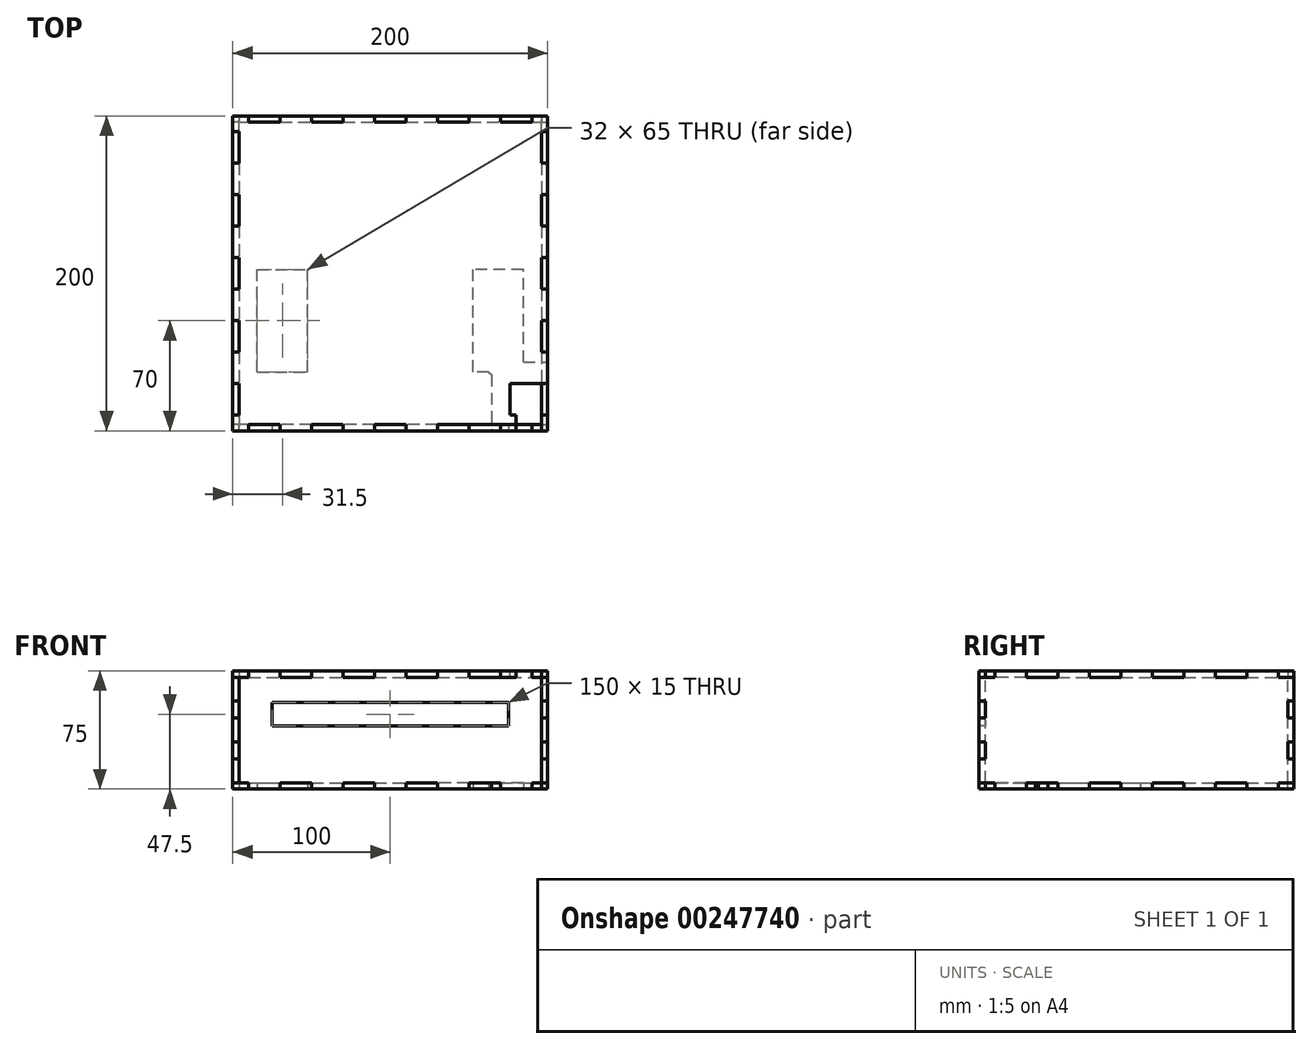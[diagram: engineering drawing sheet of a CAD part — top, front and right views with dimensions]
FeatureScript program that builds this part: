
annotation { "Feature Type Name" : "Feature", "Feature Type Description" : "" }
export const myFeature = defineFeature(function(context is Context, id is Id, definition is map)
    precondition{}
    {
        {
            var Q0;
            Q0=qCreatedBy(makeId("Top.planeOp"),FACE);
            var sketch = newSketch(context, id + "F0", { "sketchPlane" : qUnion([Q0])});
            skLineSegment(sketch, "E0.bottom", {"start": v(100, -100) * mm, "end": v(-100, -100) * mm});
            skLineSegment(sketch, "E0.top", {"start": v(100, 100) * mm, "end": v(-100, 100) * mm});
            skLineSegment(sketch, "E0.left", {"start": v(100, -100) * mm, "end": v(100, 100) * mm});
            skLineSegment(sketch, "E0.right", {"start": v(-100, -100) * mm, "end": v(-100, 100) * mm});
            skPoint(sketch, "E0.middle", {"position": v(0, 0) * mm});
            skLineSegment(sketch, "E1", {"start": v(0, 100) * mm, "end": v(0, 96) * mm});
            skLineSegment(sketch, "E2", {"start": v(0, 96) * mm, "end": v(10, 96) * mm});
            skLineSegment(sketch, "E3", {"start": v(10, 96) * mm, "end": v(10, 100) * mm});
            skLineSegment(sketch, "E4.MirrorCS", {"start": v(0, 96) * mm, "end": v(-10, 96) * mm});
            skLineSegment(sketch, "E5.MirrorCS", {"start": v(-10, 96) * mm, "end": v(-10, 100) * mm});
            skLineSegment(sketch, "E6.1.0.0", {"start": v(30, 96) * mm, "end": v(30, 100) * mm});
            skLineSegment(sketch, "E6.1.0.1", {"start": v(40, 96) * mm, "end": v(30, 96) * mm});
            skLineSegment(sketch, "E6.1.0.2", {"start": v(40, 96) * mm, "end": v(50, 96) * mm});
            skLineSegment(sketch, "E6.1.0.3", {"start": v(50, 96) * mm, "end": v(50, 100) * mm});
            skLineSegment(sketch, "E6.2.0.0", {"start": v(70, 96) * mm, "end": v(70, 100) * mm});
            skLineSegment(sketch, "E6.2.0.1", {"start": v(80, 96) * mm, "end": v(70, 96) * mm});
            skLineSegment(sketch, "E6.2.0.2", {"start": v(80, 96) * mm, "end": v(90, 96) * mm});
            skLineSegment(sketch, "E6.2.0.3", {"start": v(90, 96) * mm, "end": v(90, 100) * mm});
            skLineSegment(sketch, "E6.direction1", {"start": v(-10, 96) * mm, "end": v(30, 96) * mm, "construction": true});
            skLineSegment(sketch, "E7.MirrorCS", {"start": v(-50, 96) * mm, "end": v(-50, 100) * mm});
            skLineSegment(sketch, "E8.MirrorCS", {"start": v(-30, 96) * mm, "end": v(-30, 100) * mm});
            skLineSegment(sketch, "E9.MirrorCS", {"start": v(-70, 96) * mm, "end": v(-70, 100) * mm});
            skLineSegment(sketch, "E10.MirrorCS", {"start": v(-90, 96) * mm, "end": v(-90, 100) * mm});
            skLineSegment(sketch, "E11.MirrorCS", {"start": v(-40, 96) * mm, "end": v(-30, 96) * mm});
            skLineSegment(sketch, "E12.MirrorCS", {"start": v(-40, 96) * mm, "end": v(-50, 96) * mm});
            skLineSegment(sketch, "E13.MirrorCS", {"start": v(-80, 96) * mm, "end": v(-70, 96) * mm});
            skLineSegment(sketch, "E14.MirrorCS", {"start": v(-80, 96) * mm, "end": v(-90, 96) * mm});
            skLineSegment(sketch, "E15", {"start": v(-100, 100) * mm, "end": v(100, -100) * mm});
            skLineSegment(sketch, "E16.MirrorCS", {"start": v(-96, 10) * mm, "end": v(-100, 10) * mm});
            skLineSegment(sketch, "E17.MirrorCS", {"start": v(-100, 0) * mm, "end": v(-96, 0) * mm});
            skLineSegment(sketch, "E18.MirrorCS", {"start": v(-96, -30) * mm, "end": v(-100, -30) * mm});
            skLineSegment(sketch, "E19.MirrorCS", {"start": v(-96, -10) * mm, "end": v(-100, -10) * mm});
            skLineSegment(sketch, "E20.MirrorCS", {"start": v(-96, 0) * mm, "end": v(-96, 10) * mm});
            skLineSegment(sketch, "E21.MirrorCS", {"start": v(-96, 50) * mm, "end": v(-100, 50) * mm});
            skLineSegment(sketch, "E22.MirrorCS", {"start": v(-96, 90) * mm, "end": v(-100, 90) * mm});
            skLineSegment(sketch, "E23.MirrorCS", {"start": v(-96, -90) * mm, "end": v(-100, -90) * mm});
            skLineSegment(sketch, "E24.MirrorCS", {"start": v(-96, -50) * mm, "end": v(-100, -50) * mm});
            skLineSegment(sketch, "E25.MirrorCS", {"start": v(-96, 30) * mm, "end": v(-100, 30) * mm});
            skLineSegment(sketch, "E26.MirrorCS", {"start": v(-96, 70) * mm, "end": v(-100, 70) * mm});
            skLineSegment(sketch, "E27.MirrorCS", {"start": v(-96, -70) * mm, "end": v(-100, -70) * mm});
            skLineSegment(sketch, "E28.MirrorCS", {"start": v(-96, -40) * mm, "end": v(-96, -30) * mm});
            skLineSegment(sketch, "E29.MirrorCS", {"start": v(-96, 0) * mm, "end": v(-96, -10) * mm});
            skLineSegment(sketch, "E30.MirrorCS", {"start": v(-96, 10) * mm, "end": v(-96, -30) * mm, "construction": true});
            skLineSegment(sketch, "E31.MirrorCS", {"start": v(-96, -80) * mm, "end": v(-96, -90) * mm});
            skLineSegment(sketch, "E32.MirrorCS", {"start": v(-96, 40) * mm, "end": v(-96, 50) * mm});
            skLineSegment(sketch, "E33.MirrorCS", {"start": v(-96, 80) * mm, "end": v(-96, 70) * mm});
            skLineSegment(sketch, "E34.MirrorCS", {"start": v(-96, -40) * mm, "end": v(-96, -50) * mm});
            skLineSegment(sketch, "E35.MirrorCS", {"start": v(-96, 80) * mm, "end": v(-96, 90) * mm});
            skLineSegment(sketch, "E36.MirrorCS", {"start": v(-96, 40) * mm, "end": v(-96, 30) * mm});
            skLineSegment(sketch, "E37.MirrorCS", {"start": v(-96, -80) * mm, "end": v(-96, -70) * mm});
            skLineSegment(sketch, "E38.MirrorCS", {"start": v(96, 10) * mm, "end": v(100, 10) * mm});
            skLineSegment(sketch, "E39.MirrorCS", {"start": v(96, 0) * mm, "end": v(96, 10) * mm});
            skLineSegment(sketch, "E40.MirrorCS", {"start": v(100, 0) * mm, "end": v(96, 0) * mm});
            skLineSegment(sketch, "E41.MirrorCS", {"start": v(96, -30) * mm, "end": v(100, -30) * mm});
            skLineSegment(sketch, "E42.MirrorCS", {"start": v(96, -40) * mm, "end": v(96, -30) * mm});
            skLineSegment(sketch, "E43.MirrorCS", {"start": v(96, 50) * mm, "end": v(100, 50) * mm});
            skLineSegment(sketch, "E44.MirrorCS", {"start": v(96, 30) * mm, "end": v(100, 30) * mm});
            skLineSegment(sketch, "E45.MirrorCS", {"start": v(96, 80) * mm, "end": v(96, 90) * mm});
            skLineSegment(sketch, "E46.MirrorCS", {"start": v(96, -50) * mm, "end": v(100, -50) * mm});
            skLineSegment(sketch, "E47.MirrorCS", {"start": v(96, 40) * mm, "end": v(96, 50) * mm});
            skLineSegment(sketch, "E48.MirrorCS", {"start": v(96, -70) * mm, "end": v(100, -70) * mm});
            skLineSegment(sketch, "E49.MirrorCS", {"start": v(96, -10) * mm, "end": v(100, -10) * mm});
            skLineSegment(sketch, "E50.MirrorCS", {"start": v(96, -90) * mm, "end": v(100, -90) * mm});
            skLineSegment(sketch, "E51.MirrorCS", {"start": v(96, -80) * mm, "end": v(96, -90) * mm});
            skLineSegment(sketch, "E52.MirrorCS", {"start": v(96, 70) * mm, "end": v(100, 70) * mm});
            skLineSegment(sketch, "E53.MirrorCS", {"start": v(96, 80) * mm, "end": v(96, 70) * mm});
            skLineSegment(sketch, "E54.MirrorCS", {"start": v(96, 90) * mm, "end": v(100, 90) * mm});
            skLineSegment(sketch, "E55.MirrorCS", {"start": v(96, -40) * mm, "end": v(96, -50) * mm});
            skLineSegment(sketch, "E56.MirrorCS", {"start": v(96, 0) * mm, "end": v(96, -10) * mm});
            skLineSegment(sketch, "E57.MirrorCS", {"start": v(96, -80) * mm, "end": v(96, -70) * mm});
            skLineSegment(sketch, "E58.MirrorCS", {"start": v(96, 40) * mm, "end": v(96, 30) * mm});
            skLineSegment(sketch, "E59.MirrorCS", {"start": v(96, 10) * mm, "end": v(96, -30) * mm, "construction": true});
            skLineSegment(sketch, "E60", {"start": v(0, -100) * mm, "end": v(0, -96) * mm});
            skLineSegment(sketch, "E61", {"start": v(0, -96) * mm, "end": v(10, -96) * mm});
            skLineSegment(sketch, "E62", {"start": v(10, -96) * mm, "end": v(10, -100) * mm});
            skLineSegment(sketch, "E63.MirrorCS", {"start": v(0, -96) * mm, "end": v(-10, -96) * mm});
            skLineSegment(sketch, "E64.MirrorCS", {"start": v(-10, -96) * mm, "end": v(-10, -100) * mm});
            skLineSegment(sketch, "E65.1.0.0", {"start": v(30, -96) * mm, "end": v(30, -100) * mm});
            skLineSegment(sketch, "E65.1.0.1", {"start": v(40, -96) * mm, "end": v(30, -96) * mm});
            skLineSegment(sketch, "E65.1.0.2", {"start": v(40, -96) * mm, "end": v(50, -96) * mm});
            skLineSegment(sketch, "E65.1.0.3", {"start": v(50, -96) * mm, "end": v(50, -100) * mm});
            skLineSegment(sketch, "E65.2.0.0", {"start": v(70, -96) * mm, "end": v(70, -100) * mm});
            skLineSegment(sketch, "E65.2.0.1", {"start": v(80, -96) * mm, "end": v(70, -96) * mm});
            skLineSegment(sketch, "E65.2.0.2", {"start": v(80, -96) * mm, "end": v(90, -96) * mm});
            skLineSegment(sketch, "E65.2.0.3", {"start": v(90, -96) * mm, "end": v(90, -100) * mm});
            skLineSegment(sketch, "E65.direction1", {"start": v(-10, -100) * mm, "end": v(30, -100) * mm, "construction": true});
            skLineSegment(sketch, "E66.MirrorCS", {"start": v(-40, -96) * mm, "end": v(-50, -96) * mm});
            skLineSegment(sketch, "E67.MirrorCS", {"start": v(-40, -96) * mm, "end": v(-30, -96) * mm});
            skLineSegment(sketch, "E68.MirrorCS", {"start": v(-80, -96) * mm, "end": v(-70, -96) * mm});
            skLineSegment(sketch, "E69.MirrorCS", {"start": v(-80, -96) * mm, "end": v(-90, -96) * mm});
            skLineSegment(sketch, "E70.MirrorCS", {"start": v(-70, -96) * mm, "end": v(-70, -100) * mm});
            skLineSegment(sketch, "E71.MirrorCS", {"start": v(-90, -96) * mm, "end": v(-90, -100) * mm});
            skLineSegment(sketch, "E72.MirrorCS", {"start": v(-30, -96) * mm, "end": v(-30, -100) * mm});
            skLineSegment(sketch, "E73.MirrorCS", {"start": v(-50, -96) * mm, "end": v(-50, -100) * mm});
            skLineSegment(sketch, "E74.bottom", {"start": v(84.5, -62.5) * mm, "end": v(52.5, -62.5) * mm});
            skLineSegment(sketch, "E74.top", {"start": v(84.5, 2.5) * mm, "end": v(52.5, 2.5) * mm});
            skLineSegment(sketch, "E74.left", {"start": v(84.5, -62.5) * mm, "end": v(84.5, 2.5) * mm});
            skLineSegment(sketch, "E74.right", {"start": v(52.5, -62.5) * mm, "end": v(52.5, 2.5) * mm});
            skPoint(sketch, "E74.middle", {"position": v(68.5, -30) * mm});
            skLineSegment(sketch, "E75", {"start": v(0, 96) * mm, "end": v(0, -96) * mm});
            skLineSegment(sketch, "E76.MirrorCS", {"start": v(-52.5, -62.5) * mm, "end": v(-52.5, 2.5) * mm});
            skLineSegment(sketch, "E77.MirrorCS", {"start": v(-84.5, 2.5) * mm, "end": v(-52.5, 2.5) * mm});
            skLineSegment(sketch, "E78.MirrorCS", {"start": v(-84.5, -62.5) * mm, "end": v(-84.5, 2.5) * mm});
            skLineSegment(sketch, "E79.MirrorCS", {"start": v(-84.5, -62.5) * mm, "end": v(-52.5, -62.5) * mm});
            skLineSegment(sketch, "E80", {"start": v(64.36, -62.5) * mm, "end": v(64.36, -100) * mm});
            skLineSegment(sketch, "E81", {"start": v(84.5, -56.4) * mm, "end": v(100, -56.4) * mm});
            skSolve(sketch);
        }
        {
            var Q0;
            Q0=makeQuery(id+"F0.imprint","IMPRINT",FACE,{"disambiguationData":[TD([[makeQuery(id+"F0.imprint","IMPRINT",EDGE,{"derivedFrom":sQuery(id+"F0.wireOp",EDGE,"E2")}),-1.0]])]});
            var Q1;
            {var subQ15=sQuery(id+"F0.wireOp",EDGE,"E15");Q1=makeQuery(id+"F0.imprint","IMPRINT",FACE,{"disambiguationData":[TD([[makeQuery(id+"F0.imprint","IMPRINT",EDGE,{"derivedFrom":subQ15}),-1.0]])]});}
            var Q2;
            {var subQ5=sQuery(id+"F0.wireOp",EDGE,"E16.MirrorCS");Q2=makeQuery(id+"F0.imprint","IMPRINT",FACE,{"disambiguationData":[TD([[makeQuery(id+"F0.imprint","IMPRINT",EDGE,{"derivedFrom":subQ5}),-1.0]])]});}
            var Q3;
            {var subQ5=sQuery(id+"F0.wireOp",EDGE,"E5.MirrorCS");Q3=makeQuery(id+"F0.imprint","IMPRINT",FACE,{"disambiguationData":[TD([[makeQuery(id+"F0.imprint","IMPRINT",EDGE,{"derivedFrom":subQ5}),1.0]])]});}
            extrude(context, id + "F1", {"entities" : qUnion([Q0, Q1, Q2, Q3]), "depth" : 4 * mm});
        }
        {
            var Q0;
            Q0=makeQuery(id+"F1.opExtrude","SWEPT_FACE",FACE,{"disambiguationData":[OSD([sQuery(id+"F0.wireOp",EDGE,"E39.MirrorCS"),sQuery(id+"F0.wireOp",EDGE,"E56.MirrorCS")])]});
            var sketch = newSketch(context, id + "F2", { "sketchPlane" : qUnion([Q0])});
            skLineSegment(sketch, "E82.0.0", {"start": v(-90, 0) * mm, "end": v(-70, 0) * mm});
            skLineSegment(sketch, "E82.0.1", {"start": v(-70, 0) * mm, "end": v(-70, 4) * mm});
            skLineSegment(sketch, "E82.0.2", {"start": v(-70, 4) * mm, "end": v(-90, 4) * mm});
            skLineSegment(sketch, "E82.0.3", {"start": v(-90, 4) * mm, "end": v(-90, 0) * mm});
            skLineSegment(sketch, "E83.0.0", {"start": v(-50, 0) * mm, "end": v(-30, 0) * mm});
            skLineSegment(sketch, "E83.0.1", {"start": v(-30, 0) * mm, "end": v(-30, 4) * mm});
            skLineSegment(sketch, "E83.0.2", {"start": v(-30, 4) * mm, "end": v(-50, 4) * mm});
            skLineSegment(sketch, "E83.0.3", {"start": v(-50, 4) * mm, "end": v(-50, 0) * mm});
            skLineSegment(sketch, "E84.0.0", {"start": v(-10, 0) * mm, "end": v(10, 0) * mm});
            skLineSegment(sketch, "E84.0.1", {"start": v(10, 0) * mm, "end": v(10, 4) * mm});
            skLineSegment(sketch, "E84.0.2", {"start": v(10, 4) * mm, "end": v(-10, 4) * mm});
            skLineSegment(sketch, "E84.0.3", {"start": v(-10, 4) * mm, "end": v(-10, 0) * mm});
            skLineSegment(sketch, "E85.0.0", {"start": v(30, 0) * mm, "end": v(50, 0) * mm});
            skLineSegment(sketch, "E85.0.1", {"start": v(50, 0) * mm, "end": v(50, 4) * mm});
            skLineSegment(sketch, "E85.0.2", {"start": v(50, 4) * mm, "end": v(30, 4) * mm});
            skLineSegment(sketch, "E85.0.3", {"start": v(30, 4) * mm, "end": v(30, 0) * mm});
            skLineSegment(sketch, "E86.0.0", {"start": v(70, 0) * mm, "end": v(90, 0) * mm});
            skLineSegment(sketch, "E86.0.1", {"start": v(90, 0) * mm, "end": v(90, 4) * mm});
            skLineSegment(sketch, "E86.0.2", {"start": v(90, 4) * mm, "end": v(70, 4) * mm});
            skLineSegment(sketch, "E86.0.3", {"start": v(70, 4) * mm, "end": v(70, 0) * mm});
            skLineSegment(sketch, "E87.0.1", {"start": v(96, 0) * mm, "end": v(96, 4) * mm});
            skLineSegment(sketch, "E87.0.3", {"start": v(96, 4) * mm, "end": v(96, 0) * mm});
            skLineSegment(sketch, "E88.0.1", {"start": v(-96, 0) * mm, "end": v(-96, 4) * mm});
            skLineSegment(sketch, "E88.0.3", {"start": v(-96, 4) * mm, "end": v(-96, 0) * mm});
            skLineSegment(sketch, "E89.0.1", {"start": v(70, 4) * mm, "end": v(90, 4) * mm});
            skLineSegment(sketch, "E89.0.3", {"start": v(90, 4) * mm, "end": v(100, 4) * mm});
            skLineSegment(sketch, "E89.0.5", {"start": v(100, 4) * mm, "end": v(96, 4) * mm});
            skLineSegment(sketch, "E89.0.7", {"start": v(96, 4) * mm, "end": v(100, 4) * mm});
            skLineSegment(sketch, "E89.0.9", {"start": v(100, 4) * mm, "end": v(96, 4) * mm});
            skLineSegment(sketch, "E89.0.11", {"start": v(96, 4) * mm, "end": v(100, 4) * mm});
            skLineSegment(sketch, "E89.0.13", {"start": v(100, 4) * mm, "end": v(96, 4) * mm});
            skLineSegment(sketch, "E89.0.15", {"start": v(96, 4) * mm, "end": v(100, 4) * mm});
            skLineSegment(sketch, "E89.0.17", {"start": v(100, 4) * mm, "end": v(96, 4) * mm});
            skLineSegment(sketch, "E89.0.19", {"start": v(96, 4) * mm, "end": v(100, 4) * mm});
            skLineSegment(sketch, "E89.0.21", {"start": v(100, 4) * mm, "end": v(96, 4) * mm});
            skLineSegment(sketch, "E89.0.23", {"start": v(96, 4) * mm, "end": v(100, 4) * mm});
            skLineSegment(sketch, "E89.0.25", {"start": v(100, 4) * mm, "end": v(90, 4) * mm});
            skLineSegment(sketch, "E89.0.29", {"start": v(70, 4) * mm, "end": v(50, 4) * mm});
            skLineSegment(sketch, "E89.0.33", {"start": v(30, 4) * mm, "end": v(10, 4) * mm});
            skLineSegment(sketch, "E89.0.37", {"start": v(-10, 4) * mm, "end": v(-30, 4) * mm});
            skLineSegment(sketch, "E89.0.41", {"start": v(-50, 4) * mm, "end": v(-70, 4) * mm});
            skLineSegment(sketch, "E89.0.45", {"start": v(-90, 4) * mm, "end": v(-100, 4) * mm});
            skLineSegment(sketch, "E89.0.47", {"start": v(-100, 4) * mm, "end": v(-96, 4) * mm});
            skLineSegment(sketch, "E89.0.49", {"start": v(-96, 4) * mm, "end": v(-100, 4) * mm});
            skLineSegment(sketch, "E89.0.51", {"start": v(-100, 4) * mm, "end": v(-96, 4) * mm});
            skLineSegment(sketch, "E89.0.53", {"start": v(-96, 4) * mm, "end": v(-100, 4) * mm});
            skLineSegment(sketch, "E89.0.55", {"start": v(-100, 4) * mm, "end": v(-96, 4) * mm});
            skLineSegment(sketch, "E89.0.57", {"start": v(-96, 4) * mm, "end": v(-100, 4) * mm});
            skLineSegment(sketch, "E89.0.59", {"start": v(-100, 4) * mm, "end": v(-96, 4) * mm});
            skLineSegment(sketch, "E89.0.61", {"start": v(-96, 4) * mm, "end": v(-100, 4) * mm});
            skLineSegment(sketch, "E89.0.63", {"start": v(-100, 4) * mm, "end": v(-96, 4) * mm});
            skLineSegment(sketch, "E89.0.65", {"start": v(-96, 4) * mm, "end": v(-100, 4) * mm});
            skLineSegment(sketch, "E89.0.67", {"start": v(-100, 4) * mm, "end": v(-90, 4) * mm});
            skLineSegment(sketch, "E89.0.69", {"start": v(-90, 4) * mm, "end": v(-70, 4) * mm});
            skLineSegment(sketch, "E89.0.71", {"start": v(-50, 4) * mm, "end": v(-50, 4) * mm});
            skLineSegment(sketch, "E89.0.73", {"start": v(-50, 4) * mm, "end": v(-30, 4) * mm});
            skLineSegment(sketch, "E89.0.75", {"start": v(-30, 4) * mm, "end": v(-10, 4) * mm});
            skLineSegment(sketch, "E89.0.77", {"start": v(-10, 4) * mm, "end": v(10, 4) * mm});
            skLineSegment(sketch, "E89.0.79", {"start": v(10, 4) * mm, "end": v(30, 4) * mm});
            skLineSegment(sketch, "E89.0.81", {"start": v(30, 4) * mm, "end": v(50, 4) * mm});
            skLineSegment(sketch, "E89.0.83", {"start": v(50, 4) * mm, "end": v(70, 4) * mm});
            skLineSegment(sketch, "E90.bottom", {"start": v(-96, 4) * mm, "end": v(96, 4) * mm});
            skLineSegment(sketch, "E90.top", {"start": v(-96, 75) * mm, "end": v(96, 75) * mm});
            skLineSegment(sketch, "E90.left", {"start": v(-96, 4) * mm, "end": v(-96, 75) * mm});
            skLineSegment(sketch, "E90.right", {"start": v(96, 4) * mm, "end": v(96, 75) * mm});
            skLineSegment(sketch, "E91", {"start": v(96, 37.5) * mm, "end": v(-96, 37.5) * mm});
            skLineSegment(sketch, "E92.MirrorCS", {"start": v(-90, 71) * mm, "end": v(-90, 75) * mm});
            skLineSegment(sketch, "E93.MirrorCS", {"start": v(-30, 75) * mm, "end": v(-30, 71) * mm});
            skLineSegment(sketch, "E94.MirrorCS", {"start": v(-10, 71) * mm, "end": v(-10, 75) * mm});
            skLineSegment(sketch, "E95.MirrorCS", {"start": v(10, 75) * mm, "end": v(10, 71) * mm});
            skLineSegment(sketch, "E96.MirrorCS", {"start": v(30, 71) * mm, "end": v(30, 75) * mm});
            skLineSegment(sketch, "E97.MirrorCS", {"start": v(50, 75) * mm, "end": v(50, 71) * mm});
            skLineSegment(sketch, "E98.MirrorCS", {"start": v(70, 71) * mm, "end": v(70, 75) * mm});
            skLineSegment(sketch, "E99.MirrorCS", {"start": v(90, 75) * mm, "end": v(90, 71) * mm});
            skLineSegment(sketch, "E100.MirrorCS", {"start": v(-70, 75) * mm, "end": v(-70, 71) * mm});
            skLineSegment(sketch, "E101.MirrorCS", {"start": v(-50, 71) * mm, "end": v(-50, 75) * mm});
            skLineSegment(sketch, "E102", {"start": v(-90, 71) * mm, "end": v(-70, 71) * mm});
            skLineSegment(sketch, "E103", {"start": v(-50, 71) * mm, "end": v(-30, 71) * mm});
            skLineSegment(sketch, "E104", {"start": v(-10, 71) * mm, "end": v(10, 71) * mm});
            skLineSegment(sketch, "E105", {"start": v(30, 71) * mm, "end": v(50, 71) * mm});
            skLineSegment(sketch, "E106", {"start": v(70, 71) * mm, "end": v(90, 71) * mm});
            skLineSegment(sketch, "E107", {"start": v(-70, 71) * mm, "end": v(-50, 71) * mm});
            skLineSegment(sketch, "E108", {"start": v(-30, 71) * mm, "end": v(-10, 71) * mm});
            skLineSegment(sketch, "E109", {"start": v(10, 71) * mm, "end": v(30, 71) * mm});
            skLineSegment(sketch, "E110", {"start": v(50, 71) * mm, "end": v(70, 71) * mm});
            skLineSegment(sketch, "E111", {"start": v(-90, 71) * mm, "end": v(-96, 71) * mm});
            skLineSegment(sketch, "E112", {"start": v(90, 71) * mm, "end": v(96, 71) * mm});
            skSolve(sketch);
        }
        {
            var Q0;
            {var subQ7=sQuery(id+"F2.wireOp",EDGE,"E91");Q0=makeQuery(id+"F2.imprint","IMPRINT",FACE,{"disambiguationData":[TD([[makeQuery(id+"F2.imprint","IMPRINT",EDGE,{"derivedFrom":subQ7}),1.0]])]});}
            var Q1;
            {var subQ0=sQuery(id+"F2.wireOp",EDGE,"E91");Q1=makeQuery(id+"F2.imprint","IMPRINT",FACE,{"disambiguationData":[TD([[makeQuery(id+"F2.imprint","IMPRINT",EDGE,{"derivedFrom":subQ0}),-1.0]])]});}
            var Q2;
            {var subQ0=sQuery(id+"F2.wireOp",EDGE,"E92.MirrorCS");Q2=makeQuery(id+"F2.imprint","IMPRINT",FACE,{"disambiguationData":[TD([[makeQuery(id+"F2.imprint","IMPRINT",EDGE,{"derivedFrom":subQ0}),-1.0]])]});}
            var Q3;
            {var subQ0=sQuery(id+"F2.wireOp",EDGE,"E93.MirrorCS");Q3=makeQuery(id+"F2.imprint","IMPRINT",FACE,{"disambiguationData":[TD([[makeQuery(id+"F2.imprint","IMPRINT",EDGE,{"derivedFrom":subQ0}),-1.0]])]});}
            var Q4;
            {var subQ0=sQuery(id+"F2.wireOp",EDGE,"E94.MirrorCS");Q4=makeQuery(id+"F2.imprint","IMPRINT",FACE,{"disambiguationData":[TD([[makeQuery(id+"F2.imprint","IMPRINT",EDGE,{"derivedFrom":subQ0}),-1.0]])]});}
            var Q5;
            {var subQ0=sQuery(id+"F2.wireOp",EDGE,"E96.MirrorCS");Q5=makeQuery(id+"F2.imprint","IMPRINT",FACE,{"disambiguationData":[TD([[makeQuery(id+"F2.imprint","IMPRINT",EDGE,{"derivedFrom":subQ0}),-1.0]])]});}
            var Q6;
            {var subQ0=sQuery(id+"F2.wireOp",EDGE,"E98.MirrorCS");Q6=makeQuery(id+"F2.imprint","IMPRINT",FACE,{"disambiguationData":[TD([[makeQuery(id+"F2.imprint","IMPRINT",EDGE,{"derivedFrom":subQ0}),-1.0]])]});}
            var Q7;
            Q7=makeQuery(id+"F2.imprint","IMPRINT",FACE,{"disambiguationData":[TD([[makeQuery(id+"F2.imprint","IMPRINT",EDGE,{"derivedFrom":sQuery(id+"F2.wireOp",EDGE,"E82.0.0")}),1.0]])]});
            var Q8;
            Q8=makeQuery(id+"F2.imprint","IMPRINT",FACE,{"disambiguationData":[TD([[makeQuery(id+"F2.imprint","IMPRINT",EDGE,{"derivedFrom":sQuery(id+"F2.wireOp",EDGE,"E83.0.0")}),1.0]])]});
            var Q9;
            Q9=makeQuery(id+"F2.imprint","IMPRINT",FACE,{"disambiguationData":[TD([[makeQuery(id+"F2.imprint","IMPRINT",EDGE,{"derivedFrom":sQuery(id+"F2.wireOp",EDGE,"E85.0.0")}),1.0]])]});
            var Q10;
            Q10=makeQuery(id+"F2.imprint","IMPRINT",FACE,{"disambiguationData":[TD([[makeQuery(id+"F2.imprint","IMPRINT",EDGE,{"derivedFrom":sQuery(id+"F2.wireOp",EDGE,"E86.0.0")}),1.0]])]});
            var Q11;
            Q11=makeQuery(id+"F2.imprint","IMPRINT",FACE,{"disambiguationData":[TD([[makeQuery(id+"F2.imprint","IMPRINT",EDGE,{"derivedFrom":sQuery(id+"F2.wireOp",EDGE,"E84.0.0")}),-1.0]])]});
            extrude(context, id + "F3", {"entities" : qUnion([Q0, Q1, Q2, Q3, Q4, Q5, Q6, Q7, Q8, Q9, Q10, Q11]), "depth" : 4 * mm});
        }
        {
            var Q0;
            Q0=makeQuery(id+"F3.opExtrude","SWEPT_BODY",BODY,{"disambiguationData":[OSD([sQuery(id+"F2.wireOp",EDGE,"E82.0.0"),sQuery(id+"F2.wireOp",EDGE,"E82.0.1"),sQuery(id+"F2.wireOp",EDGE,"E82.0.3"),sQuery(id+"F2.wireOp",EDGE,"E83.0.0"),sQuery(id+"F2.wireOp",EDGE,"E83.0.1"),sQuery(id+"F2.wireOp",EDGE,"E83.0.3"),sQuery(id+"F2.wireOp",EDGE,"E84.0.0"),sQuery(id+"F2.wireOp",EDGE,"E84.0.1"),sQuery(id+"F2.wireOp",EDGE,"E84.0.3"),sQuery(id+"F2.wireOp",EDGE,"E85.0.0"),sQuery(id+"F2.wireOp",EDGE,"E85.0.1"),sQuery(id+"F2.wireOp",EDGE,"E85.0.3"),sQuery(id+"F2.wireOp",EDGE,"E86.0.0"),sQuery(id+"F2.wireOp",EDGE,"E86.0.1"),sQuery(id+"F2.wireOp",EDGE,"E86.0.3"),sQuery(id+"F2.wireOp",EDGE,"E90.bottom"),sQuery(id+"F2.wireOp",EDGE,"E90.top"),sQuery(id+"F2.wireOp",EDGE,"E90.left"),sQuery(id+"F2.wireOp",EDGE,"E90.right")])]});
            var Q1;
            Q1=qCreatedBy(makeId("Right.planeOp"),FACE);
            mirror(context, id + "F4", {"entities" : qUnion([Q0]), "mirrorPlane" : qUnion([Q1])});
        }
        {
            var Q0;
            Q0=makeQuery(id+"F1.opExtrude","SWEPT_FACE",FACE,{"disambiguationData":[OSD([sQuery(id+"F0.wireOp",EDGE,"E61"),sQuery(id+"F0.wireOp",EDGE,"E63.MirrorCS")])]});
            var sketch = newSketch(context, id + "F5", { "sketchPlane" : qUnion([Q0])});
            skLineSegment(sketch, "E113.0.0", {"start": v(100, 4) * mm, "end": v(96, 4) * mm});
            skLineSegment(sketch, "E113.0.2", {"start": v(96, 4) * mm, "end": v(100, 4) * mm});
            skLineSegment(sketch, "E113.0.4", {"start": v(100, 4) * mm, "end": v(90, 4) * mm});
            skLineSegment(sketch, "E113.0.6", {"start": v(90, 4) * mm, "end": v(70, 4) * mm});
            skLineSegment(sketch, "E113.0.8", {"start": v(70, 4) * mm, "end": v(50, 4) * mm});
            skLineSegment(sketch, "E113.0.10", {"start": v(50, 4) * mm, "end": v(30, 4) * mm});
            skLineSegment(sketch, "E113.0.12", {"start": v(30, 4) * mm, "end": v(10, 4) * mm});
            skLineSegment(sketch, "E113.0.14", {"start": v(10, 4) * mm, "end": v(-10, 4) * mm});
            skLineSegment(sketch, "E113.0.16", {"start": v(-10, 4) * mm, "end": v(-30, 4) * mm});
            skLineSegment(sketch, "E113.0.18", {"start": v(-30, 4) * mm, "end": v(-50, 4) * mm});
            skLineSegment(sketch, "E113.0.20", {"start": v(-50, 4) * mm, "end": v(-70, 4) * mm});
            skLineSegment(sketch, "E113.0.22", {"start": v(-70, 4) * mm, "end": v(-90, 4) * mm});
            skLineSegment(sketch, "E113.0.24", {"start": v(-90, 4) * mm, "end": v(-100, 4) * mm});
            skLineSegment(sketch, "E113.0.26", {"start": v(-100, 4) * mm, "end": v(-96, 4) * mm});
            skLineSegment(sketch, "E113.0.28", {"start": v(-96, 4) * mm, "end": v(-100, 4) * mm});
            skLineSegment(sketch, "E113.0.30", {"start": v(-100, 4) * mm, "end": v(-96, 4) * mm});
            skLineSegment(sketch, "E113.0.32", {"start": v(-96, 4) * mm, "end": v(-100, 4) * mm});
            skLineSegment(sketch, "E113.0.34", {"start": v(-100, 4) * mm, "end": v(-96, 4) * mm});
            skLineSegment(sketch, "E113.0.36", {"start": v(-96, 4) * mm, "end": v(-100, 4) * mm});
            skLineSegment(sketch, "E113.0.38", {"start": v(-100, 4) * mm, "end": v(-96, 4) * mm});
            skLineSegment(sketch, "E113.0.40", {"start": v(-96, 4) * mm, "end": v(-100, 4) * mm});
            skLineSegment(sketch, "E113.0.42", {"start": v(-100, 4) * mm, "end": v(-96, 4) * mm});
            skLineSegment(sketch, "E113.0.44", {"start": v(-96, 4) * mm, "end": v(-100, 4) * mm});
            skLineSegment(sketch, "E113.0.46", {"start": v(-100, 4) * mm, "end": v(-90, 4) * mm});
            skLineSegment(sketch, "E113.0.48", {"start": v(-90, 4) * mm, "end": v(-70, 4) * mm});
            skLineSegment(sketch, "E113.0.50", {"start": v(-70, 4) * mm, "end": v(-50, 4) * mm});
            skLineSegment(sketch, "E113.0.52", {"start": v(-50, 4) * mm, "end": v(-30, 4) * mm});
            skLineSegment(sketch, "E113.0.54", {"start": v(-30, 4) * mm, "end": v(-10, 4) * mm});
            skLineSegment(sketch, "E113.0.56", {"start": v(-10, 4) * mm, "end": v(10, 4) * mm});
            skLineSegment(sketch, "E113.0.58", {"start": v(10, 4) * mm, "end": v(30, 4) * mm});
            skLineSegment(sketch, "E113.0.60", {"start": v(30, 4) * mm, "end": v(50, 4) * mm});
            skLineSegment(sketch, "E113.0.62", {"start": v(50, 4) * mm, "end": v(50, 4) * mm});
            skLineSegment(sketch, "E113.0.64", {"start": v(70, 4) * mm, "end": v(90, 4) * mm});
            skLineSegment(sketch, "E113.0.66", {"start": v(90, 4) * mm, "end": v(100, 4) * mm});
            skLineSegment(sketch, "E113.0.68", {"start": v(100, 4) * mm, "end": v(96, 4) * mm});
            skLineSegment(sketch, "E113.0.70", {"start": v(96, 4) * mm, "end": v(100, 4) * mm});
            skLineSegment(sketch, "E113.0.72", {"start": v(100, 4) * mm, "end": v(96, 4) * mm});
            skLineSegment(sketch, "E113.0.74", {"start": v(96, 4) * mm, "end": v(100, 4) * mm});
            skLineSegment(sketch, "E113.0.76", {"start": v(100, 4) * mm, "end": v(96, 4) * mm});
            skLineSegment(sketch, "E113.0.78", {"start": v(96, 4) * mm, "end": v(100, 4) * mm});
            skLineSegment(sketch, "E113.0.80", {"start": v(100, 4) * mm, "end": v(96, 4) * mm});
            skLineSegment(sketch, "E113.0.82", {"start": v(96, 4) * mm, "end": v(100, 4) * mm});
            skPoint(sketch, "E114.0", {"position": v(96, 4) * mm});
            skPoint(sketch, "E115.0", {"position": v(-96, 4) * mm});
            skLineSegment(sketch, "E116.bottom", {"start": v(-96, 4) * mm, "end": v(96, 4) * mm});
            skLineSegment(sketch, "E116.top", {"start": v(-96, 4) * mm, "end": v(96, 4) * mm});
            skLineSegment(sketch, "E116.left", {"start": v(-96, 4) * mm, "end": v(-96, 4) * mm});
            skLineSegment(sketch, "E116.right", {"start": v(96, 4) * mm, "end": v(96, 4) * mm});
            skPoint(sketch, "E117.0", {"position": v(-100, 0) * mm});
            skLineSegment(sketch, "E118.0.0", {"start": v(70, 0) * mm, "end": v(90, 0) * mm});
            skLineSegment(sketch, "E118.0.1", {"start": v(90, 0) * mm, "end": v(90, 4) * mm});
            skLineSegment(sketch, "E118.0.3", {"start": v(70, 4) * mm, "end": v(70, 0) * mm});
            skLineSegment(sketch, "E119.0.0", {"start": v(30, 0) * mm, "end": v(50, 0) * mm});
            skLineSegment(sketch, "E119.0.1", {"start": v(50, 0) * mm, "end": v(50, 4) * mm});
            skLineSegment(sketch, "E119.0.3", {"start": v(30, 4) * mm, "end": v(30, 0) * mm});
            skLineSegment(sketch, "E120.0.0", {"start": v(-10, 0) * mm, "end": v(10, 0) * mm});
            skLineSegment(sketch, "E120.0.1", {"start": v(10, 0) * mm, "end": v(10, 4) * mm});
            skLineSegment(sketch, "E120.0.3", {"start": v(-10, 4) * mm, "end": v(-10, 0) * mm});
            skLineSegment(sketch, "E121.0.0", {"start": v(-50, 0) * mm, "end": v(-30, 0) * mm});
            skLineSegment(sketch, "E121.0.1", {"start": v(-30, 0) * mm, "end": v(-30, 4) * mm});
            skLineSegment(sketch, "E121.0.3", {"start": v(-50, 4) * mm, "end": v(-50, 0) * mm});
            skLineSegment(sketch, "E122.0.0", {"start": v(-90, 0) * mm, "end": v(-70, 0) * mm});
            skLineSegment(sketch, "E122.0.1", {"start": v(-70, 0) * mm, "end": v(-70, 4) * mm});
            skLineSegment(sketch, "E122.0.3", {"start": v(-90, 4) * mm, "end": v(-90, 0) * mm});
            skPoint(sketch, "E123.0", {"position": v(-96, 71) * mm});
            skPoint(sketch, "E124.0", {"position": v(-96, 75) * mm});
            skPoint(sketch, "E125.0", {"position": v(96, 75) * mm});
            skPoint(sketch, "E126.0", {"position": v(96, 71) * mm});
            skLineSegment(sketch, "E127.top", {"start": v(-96, 75) * mm, "end": v(96, 75) * mm});
            skLineSegment(sketch, "E127.left", {"start": v(-96, 4) * mm, "end": v(-96, 75) * mm});
            skLineSegment(sketch, "E127.right", {"start": v(96, 4) * mm, "end": v(96, 75) * mm});
            skLineSegment(sketch, "E128", {"start": v(-96, 37.5) * mm, "end": v(96, 37.5) * mm});
            skLineSegment(sketch, "E129.MirrorCS", {"start": v(-90, 71) * mm, "end": v(-90, 75) * mm});
            skLineSegment(sketch, "E130.MirrorCS", {"start": v(-70, 75) * mm, "end": v(-70, 71) * mm});
            skLineSegment(sketch, "E131.MirrorCS", {"start": v(-50, 71) * mm, "end": v(-50, 75) * mm});
            skLineSegment(sketch, "E132.MirrorCS", {"start": v(-30, 75) * mm, "end": v(-30, 71) * mm});
            skLineSegment(sketch, "E133.MirrorCS", {"start": v(-10, 71) * mm, "end": v(-10, 75) * mm});
            skLineSegment(sketch, "E134.MirrorCS", {"start": v(10, 75) * mm, "end": v(10, 71) * mm});
            skLineSegment(sketch, "E135.MirrorCS", {"start": v(30, 71) * mm, "end": v(30, 75) * mm});
            skLineSegment(sketch, "E136.MirrorCS", {"start": v(50, 75) * mm, "end": v(50, 71) * mm});
            skLineSegment(sketch, "E137.MirrorCS", {"start": v(70, 71) * mm, "end": v(70, 75) * mm});
            skLineSegment(sketch, "E138.MirrorCS", {"start": v(90, 75) * mm, "end": v(90, 71) * mm});
            skLineSegment(sketch, "E139", {"start": v(-90, 71) * mm, "end": v(-96, 71) * mm});
            skLineSegment(sketch, "E140", {"start": v(90, 71) * mm, "end": v(96, 71) * mm});
            skLineSegment(sketch, "E141", {"start": v(70, 71) * mm, "end": v(50, 71) * mm});
            skLineSegment(sketch, "E142", {"start": v(30, 71) * mm, "end": v(10, 71) * mm});
            skLineSegment(sketch, "E143", {"start": v(-10, 71) * mm, "end": v(-30, 71) * mm});
            skLineSegment(sketch, "E144", {"start": v(-50, 71) * mm, "end": v(-70, 71) * mm});
            skSolve(sketch);
        }
        {
            var Q0;
            Q0=makeQuery(id+"F5.imprint","IMPRINT",FACE,{"disambiguationData":[TD([[makeQuery(id+"F5.imprint","IMPRINT",EDGE,{"derivedFrom":sQuery(id+"F5.wireOp",EDGE,"E118.0.0")}),1.0]])]});
            var Q1;
            Q1=makeQuery(id+"F5.imprint","IMPRINT",FACE,{"disambiguationData":[TD([[makeQuery(id+"F5.imprint","IMPRINT",EDGE,{"derivedFrom":sQuery(id+"F5.wireOp",EDGE,"E119.0.0")}),1.0]])]});
            var Q2;
            Q2=makeQuery(id+"F5.imprint","IMPRINT",FACE,{"disambiguationData":[TD([[makeQuery(id+"F5.imprint","IMPRINT",EDGE,{"derivedFrom":sQuery(id+"F5.wireOp",EDGE,"E120.0.0")}),-1.0]])]});
            var Q3;
            Q3=makeQuery(id+"F5.imprint","IMPRINT",FACE,{"disambiguationData":[TD([[makeQuery(id+"F5.imprint","IMPRINT",EDGE,{"derivedFrom":sQuery(id+"F5.wireOp",EDGE,"E121.0.0")}),1.0]])]});
            var Q4;
            Q4=makeQuery(id+"F5.imprint","IMPRINT",FACE,{"disambiguationData":[TD([[makeQuery(id+"F5.imprint","IMPRINT",EDGE,{"derivedFrom":sQuery(id+"F5.wireOp",EDGE,"E122.0.0")}),1.0]])]});
            var Q5;
            {var subQ7=sQuery(id+"F5.wireOp",EDGE,"E128");Q5=makeQuery(id+"F5.imprint","IMPRINT",FACE,{"disambiguationData":[TD([[makeQuery(id+"F5.imprint","IMPRINT",EDGE,{"derivedFrom":subQ7}),-1.0]])]});}
            var Q6;
            {var subQ13=sQuery(id+"F5.wireOp",EDGE,"E128");Q6=makeQuery(id+"F5.imprint","IMPRINT",FACE,{"disambiguationData":[TD([[makeQuery(id+"F5.imprint","IMPRINT",EDGE,{"derivedFrom":subQ13}),1.0]])]});}
            var Q7;
            Q7=makeQuery(id+"F5.imprint","IMPRINT",FACE,{"disambiguationData":[TD([[makeQuery(id+"F5.imprint","IMPRINT",EDGE,{"derivedFrom":sQuery(id+"F5.wireOp",EDGE,"E120.0.0")}),1.0]])]});
            extrude(context, id + "F6", {"entities" : qUnion([Q0, Q1, Q2, Q3, Q4, Q5, Q6, Q7]), "depth" : 4 * mm});
        }
        {
            var Q0;
            Q0=makeQuery(id+"F6.opExtrude","SWEPT_BODY",BODY,{"disambiguationData":[OSD([sQuery(id+"F5.wireOp",EDGE,"E116.bottom"),sQuery(id+"F5.wireOp",EDGE,"E116.top"),sQuery(id+"F5.wireOp",EDGE,"E116.left"),sQuery(id+"F5.wireOp",EDGE,"E116.right"),sQuery(id+"F5.wireOp",EDGE,"E118.0.0"),sQuery(id+"F5.wireOp",EDGE,"E118.0.1"),sQuery(id+"F5.wireOp",EDGE,"E118.0.3"),sQuery(id+"F5.wireOp",EDGE,"E119.0.0"),sQuery(id+"F5.wireOp",EDGE,"E119.0.1"),sQuery(id+"F5.wireOp",EDGE,"E119.0.3"),sQuery(id+"F5.wireOp",EDGE,"E120.0.0"),sQuery(id+"F5.wireOp",EDGE,"E120.0.1"),sQuery(id+"F5.wireOp",EDGE,"E120.0.3"),sQuery(id+"F5.wireOp",EDGE,"E121.0.0"),sQuery(id+"F5.wireOp",EDGE,"E121.0.1"),sQuery(id+"F5.wireOp",EDGE,"E121.0.3"),sQuery(id+"F5.wireOp",EDGE,"E122.0.0"),sQuery(id+"F5.wireOp",EDGE,"E122.0.1"),sQuery(id+"F5.wireOp",EDGE,"E122.0.3")])]});
            var Q1;
            Q1=qCreatedBy(makeId("Front.planeOp"),FACE);
            mirror(context, id + "F7", {"entities" : qUnion([Q0]), "mirrorPlane" : qUnion([Q1])});
        }
        {
            var Q0;
            Q0=makeQuery(id+"F4.opPattern","COPY",FACE,{"derivedFrom":makeQuery(id+"F3.opExtrude","SWEPT_FACE",FACE,{"disambiguationData":[OSD([sQuery(id+"F2.wireOp",EDGE,"E90.top")])]}),"instanceName":"1"});
            var sketch = newSketch(context, id + "F8", { "sketchPlane" : qUnion([Q0])});
            skLineSegment(sketch, "E145.0.0", {"start": v(100, 70) * mm, "end": v(96, 70) * mm});
            skLineSegment(sketch, "E145.0.1", {"start": v(96, 70) * mm, "end": v(96, 90) * mm});
            skLineSegment(sketch, "E145.0.2", {"start": v(96, 90) * mm, "end": v(100, 90) * mm});
            skLineSegment(sketch, "E145.0.3", {"start": v(100, 90) * mm, "end": v(100, 100) * mm});
            skLineSegment(sketch, "E145.0.4", {"start": v(100, 100) * mm, "end": v(90, 100) * mm});
            skLineSegment(sketch, "E145.0.5", {"start": v(90, 100) * mm, "end": v(90, 96) * mm});
            skLineSegment(sketch, "E145.0.6", {"start": v(90, 96) * mm, "end": v(70, 96) * mm});
            skLineSegment(sketch, "E145.0.7", {"start": v(70, 96) * mm, "end": v(70, 100) * mm});
            skLineSegment(sketch, "E145.0.8", {"start": v(70, 100) * mm, "end": v(50, 100) * mm});
            skLineSegment(sketch, "E145.0.9", {"start": v(50, 100) * mm, "end": v(50, 96) * mm});
            skLineSegment(sketch, "E145.0.10", {"start": v(50, 96) * mm, "end": v(30, 96) * mm});
            skLineSegment(sketch, "E145.0.11", {"start": v(30, 96) * mm, "end": v(30, 100) * mm});
            skLineSegment(sketch, "E145.0.12", {"start": v(30, 100) * mm, "end": v(10, 100) * mm});
            skLineSegment(sketch, "E145.0.13", {"start": v(10, 100) * mm, "end": v(10, 96) * mm});
            skLineSegment(sketch, "E145.0.14", {"start": v(10, 96) * mm, "end": v(-10, 96) * mm});
            skLineSegment(sketch, "E145.0.15", {"start": v(-10, 96) * mm, "end": v(-10, 100) * mm});
            skLineSegment(sketch, "E145.0.16", {"start": v(-10, 100) * mm, "end": v(-30, 100) * mm});
            skLineSegment(sketch, "E145.0.17", {"start": v(-30, 100) * mm, "end": v(-30, 96) * mm});
            skLineSegment(sketch, "E145.0.18", {"start": v(-30, 96) * mm, "end": v(-50, 96) * mm});
            skLineSegment(sketch, "E145.0.19", {"start": v(-50, 96) * mm, "end": v(-50, 100) * mm});
            skLineSegment(sketch, "E145.0.20", {"start": v(-50, 100) * mm, "end": v(-70, 100) * mm});
            skLineSegment(sketch, "E145.0.21", {"start": v(-70, 100) * mm, "end": v(-70, 96) * mm});
            skLineSegment(sketch, "E145.0.22", {"start": v(-70, 96) * mm, "end": v(-90, 96) * mm});
            skLineSegment(sketch, "E145.0.23", {"start": v(-90, 96) * mm, "end": v(-90, 100) * mm});
            skLineSegment(sketch, "E145.0.24", {"start": v(-90, 100) * mm, "end": v(-100, 100) * mm});
            skLineSegment(sketch, "E145.0.25", {"start": v(-100, 100) * mm, "end": v(-100, 90) * mm});
            skLineSegment(sketch, "E145.0.26", {"start": v(-100, 90) * mm, "end": v(-96, 90) * mm});
            skLineSegment(sketch, "E145.0.27", {"start": v(-96, 90) * mm, "end": v(-96, 70) * mm});
            skLineSegment(sketch, "E145.0.28", {"start": v(-96, 70) * mm, "end": v(-100, 70) * mm});
            skLineSegment(sketch, "E145.0.29", {"start": v(-100, 70) * mm, "end": v(-100, 50) * mm});
            skLineSegment(sketch, "E145.0.30", {"start": v(-100, 50) * mm, "end": v(-96, 50) * mm});
            skLineSegment(sketch, "E145.0.31", {"start": v(-96, 50) * mm, "end": v(-96, 30) * mm});
            skLineSegment(sketch, "E145.0.32", {"start": v(-96, 30) * mm, "end": v(-100, 30) * mm});
            skLineSegment(sketch, "E145.0.33", {"start": v(-100, 30) * mm, "end": v(-100, 10) * mm});
            skLineSegment(sketch, "E145.0.34", {"start": v(-100, 10) * mm, "end": v(-96, 10) * mm});
            skLineSegment(sketch, "E145.0.35", {"start": v(-96, 10) * mm, "end": v(-96, -10) * mm});
            skLineSegment(sketch, "E145.0.36", {"start": v(-96, -10) * mm, "end": v(-100, -10) * mm});
            skLineSegment(sketch, "E145.0.37", {"start": v(-100, -10) * mm, "end": v(-100, -30) * mm});
            skLineSegment(sketch, "E145.0.38", {"start": v(-100, -30) * mm, "end": v(-96, -30) * mm});
            skLineSegment(sketch, "E145.0.39", {"start": v(-96, -30) * mm, "end": v(-96, -50) * mm});
            skLineSegment(sketch, "E145.0.40", {"start": v(-96, -50) * mm, "end": v(-100, -50) * mm});
            skLineSegment(sketch, "E145.0.41", {"start": v(-100, -50) * mm, "end": v(-100, -70) * mm});
            skLineSegment(sketch, "E145.0.42", {"start": v(-100, -70) * mm, "end": v(-96, -70) * mm});
            skLineSegment(sketch, "E145.0.43", {"start": v(-96, -70) * mm, "end": v(-96, -90) * mm});
            skLineSegment(sketch, "E145.0.44", {"start": v(-96, -90) * mm, "end": v(-100, -90) * mm});
            skLineSegment(sketch, "E145.0.45", {"start": v(-100, -90) * mm, "end": v(-100, -100) * mm});
            skLineSegment(sketch, "E145.0.46", {"start": v(-100, -100) * mm, "end": v(-90, -100) * mm});
            skLineSegment(sketch, "E145.0.47", {"start": v(-90, -100) * mm, "end": v(-90, -96) * mm});
            skLineSegment(sketch, "E145.0.48", {"start": v(-90, -96) * mm, "end": v(-70, -96) * mm});
            skLineSegment(sketch, "E145.0.49", {"start": v(-70, -96) * mm, "end": v(-70, -100) * mm});
            skLineSegment(sketch, "E145.0.50", {"start": v(-70, -100) * mm, "end": v(-50, -100) * mm});
            skLineSegment(sketch, "E145.0.51", {"start": v(-50, -100) * mm, "end": v(-50, -96) * mm});
            skLineSegment(sketch, "E145.0.52", {"start": v(-50, -96) * mm, "end": v(-30, -96) * mm});
            skLineSegment(sketch, "E145.0.53", {"start": v(-30, -96) * mm, "end": v(-30, -100) * mm});
            skLineSegment(sketch, "E145.0.54", {"start": v(-30, -100) * mm, "end": v(-10, -100) * mm});
            skLineSegment(sketch, "E145.0.55", {"start": v(-10, -100) * mm, "end": v(-10, -96) * mm});
            skLineSegment(sketch, "E145.0.56", {"start": v(-10, -96) * mm, "end": v(10, -96) * mm});
            skLineSegment(sketch, "E145.0.57", {"start": v(10, -96) * mm, "end": v(10, -100) * mm});
            skLineSegment(sketch, "E145.0.58", {"start": v(10, -100) * mm, "end": v(30, -100) * mm});
            skLineSegment(sketch, "E145.0.59", {"start": v(30, -100) * mm, "end": v(30, -96) * mm});
            skLineSegment(sketch, "E145.0.60", {"start": v(30, -96) * mm, "end": v(50, -96) * mm});
            skLineSegment(sketch, "E145.0.61", {"start": v(50, -96) * mm, "end": v(50, -100) * mm});
            skLineSegment(sketch, "E145.0.62", {"start": v(50, -100) * mm, "end": v(50, -100) * mm});
            skLineSegment(sketch, "E145.0.63", {"start": v(50, -100) * mm, "end": v(50, -96) * mm});
            skLineSegment(sketch, "E145.0.64", {"start": v(50, -96) * mm, "end": v(70, -96) * mm});
            skLineSegment(sketch, "E145.0.65", {"start": v(70, -96) * mm, "end": v(70, -100) * mm});
            skLineSegment(sketch, "E145.0.66", {"start": v(70, -100) * mm, "end": v(80, -100) * mm});
            skLineSegment(sketch, "E145.0.67", {"start": v(80, -100) * mm, "end": v(80, -90) * mm});
            skLineSegment(sketch, "E145.0.68", {"start": v(80, -90) * mm, "end": v(76, -90) * mm});
            skLineSegment(sketch, "E145.0.69", {"start": v(76, -90) * mm, "end": v(76, -70) * mm});
            skLineSegment(sketch, "E145.0.70", {"start": v(76, -70) * mm, "end": v(100, -70) * mm});
            skLineSegment(sketch, "E145.0.71", {"start": v(100, -70) * mm, "end": v(100, -50) * mm});
            skLineSegment(sketch, "E145.0.72", {"start": v(100, -50) * mm, "end": v(96, -50) * mm});
            skLineSegment(sketch, "E145.0.73", {"start": v(96, -50) * mm, "end": v(96, -30) * mm});
            skLineSegment(sketch, "E145.0.74", {"start": v(96, -30) * mm, "end": v(100, -30) * mm});
            skLineSegment(sketch, "E145.0.75", {"start": v(100, -30) * mm, "end": v(100, -10) * mm});
            skLineSegment(sketch, "E145.0.76", {"start": v(100, -10) * mm, "end": v(96, -10) * mm});
            skLineSegment(sketch, "E145.0.77", {"start": v(96, -10) * mm, "end": v(96, 10) * mm});
            skLineSegment(sketch, "E145.0.78", {"start": v(96, 10) * mm, "end": v(100, 10) * mm});
            skLineSegment(sketch, "E145.0.79", {"start": v(100, 10) * mm, "end": v(100, 30) * mm});
            skLineSegment(sketch, "E145.0.80", {"start": v(100, 30) * mm, "end": v(96, 30) * mm});
            skLineSegment(sketch, "E145.0.81", {"start": v(96, 30) * mm, "end": v(96, 50) * mm});
            skLineSegment(sketch, "E145.0.82", {"start": v(96, 50) * mm, "end": v(100, 50) * mm});
            skLineSegment(sketch, "E145.0.83", {"start": v(100, 50) * mm, "end": v(100, 70) * mm});
            skSolve(sketch);
        }
        {
            var Q0;
            Q0 = qSketchRegion(id + "F8", true);
            extrude(context, id + "F9", {"entities" : qUnion([Q0]), "oppositeDirection" : true, "depth" : 4 * mm});
        }
        {
            var Q0;
            Q0=makeQuery(id+"F6.opExtrude","CAP_FACE",FACE,{"disambiguationData":[OSD([sQuery(id+"F5.wireOp",EDGE,"E118.0.0"),sQuery(id+"F5.wireOp",EDGE,"E118.0.1"),sQuery(id+"F5.wireOp",EDGE,"E118.0.3"),sQuery(id+"F5.wireOp",EDGE,"E119.0.0"),sQuery(id+"F5.wireOp",EDGE,"E119.0.1"),sQuery(id+"F5.wireOp",EDGE,"E119.0.3"),sQuery(id+"F5.wireOp",EDGE,"E120.0.0"),sQuery(id+"F5.wireOp",EDGE,"E120.0.1"),sQuery(id+"F5.wireOp",EDGE,"E120.0.3"),sQuery(id+"F5.wireOp",EDGE,"E121.0.0"),sQuery(id+"F5.wireOp",EDGE,"E121.0.1"),sQuery(id+"F5.wireOp",EDGE,"E121.0.3"),sQuery(id+"F5.wireOp",EDGE,"E122.0.0"),sQuery(id+"F5.wireOp",EDGE,"E122.0.1"),sQuery(id+"F5.wireOp",EDGE,"E122.0.3"),sQuery(id+"F5.wireOp",EDGE,"E116.bottom"),sQuery(id+"F5.wireOp",EDGE,"E127.top"),sQuery(id+"F5.wireOp",EDGE,"E127.left"),sQuery(id+"F5.wireOp",EDGE,"E127.right"),sQuery(id+"F5.wireOp",EDGE,"E129.MirrorCS"),sQuery(id+"F5.wireOp",EDGE,"E130.MirrorCS"),sQuery(id+"F5.wireOp",EDGE,"E131.MirrorCS"),sQuery(id+"F5.wireOp",EDGE,"E132.MirrorCS"),sQuery(id+"F5.wireOp",EDGE,"E133.MirrorCS"),sQuery(id+"F5.wireOp",EDGE,"E134.MirrorCS"),sQuery(id+"F5.wireOp",EDGE,"E135.MirrorCS"),sQuery(id+"F5.wireOp",EDGE,"E136.MirrorCS"),sQuery(id+"F5.wireOp",EDGE,"E137.MirrorCS"),sQuery(id+"F5.wireOp",EDGE,"E138.MirrorCS"),sQuery(id+"F5.wireOp",EDGE,"E139"),sQuery(id+"F5.wireOp",EDGE,"E140"),sQuery(id+"F5.wireOp",EDGE,"E141"),sQuery(id+"F5.wireOp",EDGE,"E142"),sQuery(id+"F5.wireOp",EDGE,"E143"),sQuery(id+"F5.wireOp",EDGE,"E144")])],"isStart":false});
            var sketch = newSketch(context, id + "F10", { "sketchPlane" : qUnion([Q0])});
            skSolve(sketch);
        }
        {
            var Q0;
            Q0=makeQuery(id+"F3.opExtrude","SWEPT_FACE",FACE,{"disambiguationData":[OSD([sQuery(id+"F2.wireOp",EDGE,"E90.left")])]});
            var sketch = newSketch(context, id + "F11", { "sketchPlane" : qUnion([Q0])});
            skPoint(sketch, "E146.0", {"position": v(96, 37.5) * mm});
            skPoint(sketch, "E147.0", {"position": v(100, 37.5) * mm});
            skLineSegment(sketch, "E148.0.1", {"start": v(96, 4) * mm, "end": v(100, 4) * mm});
            skLineSegment(sketch, "E148.0.2", {"start": v(100, 4) * mm, "end": v(100, 71) * mm});
            skLineSegment(sketch, "E148.0.3", {"start": v(100, 71) * mm, "end": v(96, 71) * mm});
            skLineSegment(sketch, "E149", {"start": v(96, 37.5) * mm, "end": v(100, 37.5) * mm});
            skLineSegment(sketch, "E150", {"start": v(96, 45) * mm, "end": v(100, 45) * mm});
            skLineSegment(sketch, "E151", {"start": v(96, 30) * mm, "end": v(100, 30) * mm});
            skLineSegment(sketch, "E152", {"start": v(96, 45) * mm, "end": v(96, 30) * mm});
            skLineSegment(sketch, "E153", {"start": v(100, 45) * mm, "end": v(100, 30) * mm});
            skLineSegment(sketch, "E154.0.1.0", {"start": v(96, 71) * mm, "end": v(100, 71) * mm});
            skLineSegment(sketch, "E154.0.1.1", {"start": v(96, 56) * mm, "end": v(100, 56) * mm});
            skLineSegment(sketch, "E154.0.1.2", {"start": v(96, 71) * mm, "end": v(96, 56) * mm});
            skLineSegment(sketch, "E154.0.1.3", {"start": v(100, 71) * mm, "end": v(100, 56) * mm});
            skLineSegment(sketch, "E154.direction1", {"start": v(96, 45) * mm, "end": v(121, 45) * mm, "construction": true});
            skLineSegment(sketch, "E154.direction2", {"start": v(96, 45) * mm, "end": v(96, 71) * mm, "construction": true});
            skLineSegment(sketch, "E155.MirrorCS", {"start": v(96, 4) * mm, "end": v(96, 19) * mm});
            skLineSegment(sketch, "E156.MirrorCS", {"start": v(100, 4) * mm, "end": v(96, 4) * mm});
            skLineSegment(sketch, "E157.MirrorCS", {"start": v(100, 4) * mm, "end": v(100, 19) * mm});
            skLineSegment(sketch, "E158.MirrorCS", {"start": v(96, 19) * mm, "end": v(100, 19) * mm});
            skLineSegment(sketch, "E159.MirrorCS", {"start": v(96, 30) * mm, "end": v(96, 4) * mm, "construction": true});
            skSolve(sketch);
        }
        {
            var Q0;
            Q0 = qSketchRegion(id + "F11", true);
            extrude(context, id + "F12", {"entities" : qUnion([Q0]), "depth" : 4 * mm});
        }
        {
            var Q0;
            Q0=makeQuery(id+"F12.opExtrude","SWEPT_BODY",BODY,{"disambiguationData":[OSD([sQuery(id+"F11.wireOp",EDGE,"E154.0.1.0"),sQuery(id+"F11.wireOp",EDGE,"E154.0.1.1"),sQuery(id+"F11.wireOp",EDGE,"E154.0.1.2"),sQuery(id+"F11.wireOp",EDGE,"E154.0.1.3")])]});
            var Q1;
            Q1=makeQuery(id+"F12.opExtrude","SWEPT_BODY",BODY,{"disambiguationData":[OSD([sQuery(id+"F11.wireOp",EDGE,"E150"),sQuery(id+"F11.wireOp",EDGE,"E152"),sQuery(id+"F11.wireOp",EDGE,"E153"),sQuery(id+"F11.wireOp",EDGE,"E151")])]});
            var Q2;
            Q2=makeQuery(id+"F12.opExtrude","SWEPT_BODY",BODY,{"disambiguationData":[OSD([sQuery(id+"F11.wireOp",EDGE,"E155.MirrorCS"),sQuery(id+"F11.wireOp",EDGE,"E157.MirrorCS"),sQuery(id+"F11.wireOp",EDGE,"E158.MirrorCS"),sQuery(id+"F11.wireOp",EDGE,"E148.0.1")])]});
            var Q3;
            Q3=qCreatedBy(makeId("Front.planeOp"),FACE);
            mirror(context, id + "F13", {"entities" : qUnion([Q0, Q1, Q2]), "mirrorPlane" : qUnion([Q3])});
        }
        {
            var Q0;
            Q0=makeQuery(id+"F12.opExtrude","SWEPT_BODY",BODY,{"disambiguationData":[OSD([sQuery(id+"F11.wireOp",EDGE,"E154.0.1.0"),sQuery(id+"F11.wireOp",EDGE,"E154.0.1.1"),sQuery(id+"F11.wireOp",EDGE,"E154.0.1.2"),sQuery(id+"F11.wireOp",EDGE,"E154.0.1.3")])]});
            var Q1;
            Q1=makeQuery(id+"F12.opExtrude","SWEPT_BODY",BODY,{"disambiguationData":[OSD([sQuery(id+"F11.wireOp",EDGE,"E150"),sQuery(id+"F11.wireOp",EDGE,"E152"),sQuery(id+"F11.wireOp",EDGE,"E153"),sQuery(id+"F11.wireOp",EDGE,"E151")])]});
            var Q2;
            Q2=makeQuery(id+"F12.opExtrude","SWEPT_BODY",BODY,{"disambiguationData":[OSD([sQuery(id+"F11.wireOp",EDGE,"E155.MirrorCS"),sQuery(id+"F11.wireOp",EDGE,"E157.MirrorCS"),sQuery(id+"F11.wireOp",EDGE,"E158.MirrorCS"),sQuery(id+"F11.wireOp",EDGE,"E148.0.1")])]});
            var Q3;
            Q3=makeQuery(id+"F13.opPattern","COPY",BODY,{"derivedFrom":makeQuery(id+"F12.opExtrude","SWEPT_BODY",BODY,{"disambiguationData":[OSD([sQuery(id+"F11.wireOp",EDGE,"E154.0.1.0"),sQuery(id+"F11.wireOp",EDGE,"E154.0.1.1"),sQuery(id+"F11.wireOp",EDGE,"E154.0.1.2"),sQuery(id+"F11.wireOp",EDGE,"E154.0.1.3")])]}),"instanceName":"1"});
            var Q4;
            Q4=makeQuery(id+"F13.opPattern","COPY",BODY,{"derivedFrom":makeQuery(id+"F12.opExtrude","SWEPT_BODY",BODY,{"disambiguationData":[OSD([sQuery(id+"F11.wireOp",EDGE,"E150"),sQuery(id+"F11.wireOp",EDGE,"E152"),sQuery(id+"F11.wireOp",EDGE,"E153"),sQuery(id+"F11.wireOp",EDGE,"E151")])]}),"instanceName":"1"});
            var Q5;
            Q5=makeQuery(id+"F13.opPattern","COPY",BODY,{"derivedFrom":makeQuery(id+"F12.opExtrude","SWEPT_BODY",BODY,{"disambiguationData":[OSD([sQuery(id+"F11.wireOp",EDGE,"E155.MirrorCS"),sQuery(id+"F11.wireOp",EDGE,"E157.MirrorCS"),sQuery(id+"F11.wireOp",EDGE,"E158.MirrorCS"),sQuery(id+"F11.wireOp",EDGE,"E148.0.1")])]}),"instanceName":"1"});
            var Q6;
            Q6=qCreatedBy(makeId("Right.planeOp"),FACE);
            mirror(context, id + "F14", {"entities" : qUnion([Q0, Q1, Q2, Q3, Q4, Q5]), "mirrorPlane" : qUnion([Q6])});
        }
        {
            var Q0;
            Q0=makeQuery(id+"F4.opPattern","COPY",BODY,{"derivedFrom":makeQuery(id+"F3.opExtrude","SWEPT_BODY",BODY,{"disambiguationData":[OSD([sQuery(id+"F2.wireOp",EDGE,"E82.0.0"),sQuery(id+"F2.wireOp",EDGE,"E82.0.1"),sQuery(id+"F2.wireOp",EDGE,"E82.0.3"),sQuery(id+"F2.wireOp",EDGE,"E83.0.0"),sQuery(id+"F2.wireOp",EDGE,"E83.0.1"),sQuery(id+"F2.wireOp",EDGE,"E83.0.3"),sQuery(id+"F2.wireOp",EDGE,"E84.0.0"),sQuery(id+"F2.wireOp",EDGE,"E84.0.1"),sQuery(id+"F2.wireOp",EDGE,"E84.0.3"),sQuery(id+"F2.wireOp",EDGE,"E85.0.0"),sQuery(id+"F2.wireOp",EDGE,"E85.0.1"),sQuery(id+"F2.wireOp",EDGE,"E85.0.3"),sQuery(id+"F2.wireOp",EDGE,"E86.0.0"),sQuery(id+"F2.wireOp",EDGE,"E86.0.1"),sQuery(id+"F2.wireOp",EDGE,"E86.0.3"),sQuery(id+"F2.wireOp",EDGE,"E90.bottom"),sQuery(id+"F2.wireOp",EDGE,"E90.top"),sQuery(id+"F2.wireOp",EDGE,"E90.left"),sQuery(id+"F2.wireOp",EDGE,"E90.right"),sQuery(id+"F2.wireOp",EDGE,"E92.MirrorCS"),sQuery(id+"F2.wireOp",EDGE,"E93.MirrorCS"),sQuery(id+"F2.wireOp",EDGE,"E94.MirrorCS"),sQuery(id+"F2.wireOp",EDGE,"E95.MirrorCS"),sQuery(id+"F2.wireOp",EDGE,"E96.MirrorCS"),sQuery(id+"F2.wireOp",EDGE,"E97.MirrorCS"),sQuery(id+"F2.wireOp",EDGE,"E98.MirrorCS"),sQuery(id+"F2.wireOp",EDGE,"E99.MirrorCS"),sQuery(id+"F2.wireOp",EDGE,"E100.MirrorCS"),sQuery(id+"F2.wireOp",EDGE,"E101.MirrorCS"),sQuery(id+"F2.wireOp",EDGE,"E107"),sQuery(id+"F2.wireOp",EDGE,"E108"),sQuery(id+"F2.wireOp",EDGE,"E109"),sQuery(id+"F2.wireOp",EDGE,"E110"),sQuery(id+"F2.wireOp",EDGE,"E111"),sQuery(id+"F2.wireOp",EDGE,"E112")])]}),"instanceName":"1"});
            var Q1;
            Q1=makeQuery(id+"F3.opExtrude","SWEPT_BODY",BODY,{"disambiguationData":[OSD([sQuery(id+"F2.wireOp",EDGE,"E82.0.0"),sQuery(id+"F2.wireOp",EDGE,"E82.0.1"),sQuery(id+"F2.wireOp",EDGE,"E82.0.3"),sQuery(id+"F2.wireOp",EDGE,"E83.0.0"),sQuery(id+"F2.wireOp",EDGE,"E83.0.1"),sQuery(id+"F2.wireOp",EDGE,"E83.0.3"),sQuery(id+"F2.wireOp",EDGE,"E84.0.0"),sQuery(id+"F2.wireOp",EDGE,"E84.0.1"),sQuery(id+"F2.wireOp",EDGE,"E84.0.3"),sQuery(id+"F2.wireOp",EDGE,"E85.0.0"),sQuery(id+"F2.wireOp",EDGE,"E85.0.1"),sQuery(id+"F2.wireOp",EDGE,"E85.0.3"),sQuery(id+"F2.wireOp",EDGE,"E86.0.0"),sQuery(id+"F2.wireOp",EDGE,"E86.0.1"),sQuery(id+"F2.wireOp",EDGE,"E86.0.3"),sQuery(id+"F2.wireOp",EDGE,"E90.bottom"),sQuery(id+"F2.wireOp",EDGE,"E90.top"),sQuery(id+"F2.wireOp",EDGE,"E90.left"),sQuery(id+"F2.wireOp",EDGE,"E90.right"),sQuery(id+"F2.wireOp",EDGE,"E92.MirrorCS"),sQuery(id+"F2.wireOp",EDGE,"E93.MirrorCS"),sQuery(id+"F2.wireOp",EDGE,"E94.MirrorCS"),sQuery(id+"F2.wireOp",EDGE,"E95.MirrorCS"),sQuery(id+"F2.wireOp",EDGE,"E96.MirrorCS"),sQuery(id+"F2.wireOp",EDGE,"E97.MirrorCS"),sQuery(id+"F2.wireOp",EDGE,"E98.MirrorCS"),sQuery(id+"F2.wireOp",EDGE,"E99.MirrorCS"),sQuery(id+"F2.wireOp",EDGE,"E100.MirrorCS"),sQuery(id+"F2.wireOp",EDGE,"E101.MirrorCS"),sQuery(id+"F2.wireOp",EDGE,"E107"),sQuery(id+"F2.wireOp",EDGE,"E108"),sQuery(id+"F2.wireOp",EDGE,"E109"),sQuery(id+"F2.wireOp",EDGE,"E110"),sQuery(id+"F2.wireOp",EDGE,"E111"),sQuery(id+"F2.wireOp",EDGE,"E112")])]});
            var Q2;
            Q2=makeQuery(id+"F14.opPattern","COPY",BODY,{"derivedFrom":makeQuery(id+"F13.opPattern","COPY",BODY,{"derivedFrom":makeQuery(id+"F12.opExtrude","SWEPT_BODY",BODY,{"disambiguationData":[OSD([sQuery(id+"F11.wireOp",EDGE,"E154.0.1.0"),sQuery(id+"F11.wireOp",EDGE,"E154.0.1.1"),sQuery(id+"F11.wireOp",EDGE,"E154.0.1.2"),sQuery(id+"F11.wireOp",EDGE,"E154.0.1.3")])]}),"instanceName":"1"}),"instanceName":"1"});
            var Q3;
            Q3=makeQuery(id+"F14.opPattern","COPY",BODY,{"derivedFrom":makeQuery(id+"F13.opPattern","COPY",BODY,{"derivedFrom":makeQuery(id+"F12.opExtrude","SWEPT_BODY",BODY,{"disambiguationData":[OSD([sQuery(id+"F11.wireOp",EDGE,"E150"),sQuery(id+"F11.wireOp",EDGE,"E152"),sQuery(id+"F11.wireOp",EDGE,"E153"),sQuery(id+"F11.wireOp",EDGE,"E151")])]}),"instanceName":"1"}),"instanceName":"1"});
            var Q4;
            Q4=makeQuery(id+"F14.opPattern","COPY",BODY,{"derivedFrom":makeQuery(id+"F13.opPattern","COPY",BODY,{"derivedFrom":makeQuery(id+"F12.opExtrude","SWEPT_BODY",BODY,{"disambiguationData":[OSD([sQuery(id+"F11.wireOp",EDGE,"E155.MirrorCS"),sQuery(id+"F11.wireOp",EDGE,"E157.MirrorCS"),sQuery(id+"F11.wireOp",EDGE,"E158.MirrorCS"),sQuery(id+"F11.wireOp",EDGE,"E148.0.1")])]}),"instanceName":"1"}),"instanceName":"1"});
            var Q5;
            Q5=makeQuery(id+"F14.opPattern","COPY",BODY,{"derivedFrom":makeQuery(id+"F12.opExtrude","SWEPT_BODY",BODY,{"disambiguationData":[OSD([sQuery(id+"F11.wireOp",EDGE,"E154.0.1.0"),sQuery(id+"F11.wireOp",EDGE,"E154.0.1.1"),sQuery(id+"F11.wireOp",EDGE,"E154.0.1.2"),sQuery(id+"F11.wireOp",EDGE,"E154.0.1.3")])]}),"instanceName":"1"});
            var Q6;
            Q6=makeQuery(id+"F14.opPattern","COPY",BODY,{"derivedFrom":makeQuery(id+"F12.opExtrude","SWEPT_BODY",BODY,{"disambiguationData":[OSD([sQuery(id+"F11.wireOp",EDGE,"E150"),sQuery(id+"F11.wireOp",EDGE,"E152"),sQuery(id+"F11.wireOp",EDGE,"E153"),sQuery(id+"F11.wireOp",EDGE,"E151")])]}),"instanceName":"1"});
            var Q7;
            Q7=makeQuery(id+"F14.opPattern","COPY",BODY,{"derivedFrom":makeQuery(id+"F12.opExtrude","SWEPT_BODY",BODY,{"disambiguationData":[OSD([sQuery(id+"F11.wireOp",EDGE,"E155.MirrorCS"),sQuery(id+"F11.wireOp",EDGE,"E157.MirrorCS"),sQuery(id+"F11.wireOp",EDGE,"E158.MirrorCS"),sQuery(id+"F11.wireOp",EDGE,"E148.0.1")])]}),"instanceName":"1"});
            booleanBodies(context, id + "F15", {"operationType" : BooleanOperationType.UNION, "tools" : qUnion([Q0, Q1, Q2, Q3, Q4, Q5, Q6, Q7])});
        }
        {
            var Q0;
            Q0=makeQuery(id+"F3.opExtrude","SWEPT_BODY",BODY,{"disambiguationData":[OSD([sQuery(id+"F2.wireOp",EDGE,"E82.0.0"),sQuery(id+"F2.wireOp",EDGE,"E82.0.1"),sQuery(id+"F2.wireOp",EDGE,"E82.0.3"),sQuery(id+"F2.wireOp",EDGE,"E83.0.0"),sQuery(id+"F2.wireOp",EDGE,"E83.0.1"),sQuery(id+"F2.wireOp",EDGE,"E83.0.3"),sQuery(id+"F2.wireOp",EDGE,"E84.0.0"),sQuery(id+"F2.wireOp",EDGE,"E84.0.1"),sQuery(id+"F2.wireOp",EDGE,"E84.0.3"),sQuery(id+"F2.wireOp",EDGE,"E85.0.0"),sQuery(id+"F2.wireOp",EDGE,"E85.0.1"),sQuery(id+"F2.wireOp",EDGE,"E85.0.3"),sQuery(id+"F2.wireOp",EDGE,"E86.0.0"),sQuery(id+"F2.wireOp",EDGE,"E86.0.1"),sQuery(id+"F2.wireOp",EDGE,"E86.0.3"),sQuery(id+"F2.wireOp",EDGE,"E90.bottom"),sQuery(id+"F2.wireOp",EDGE,"E90.top"),sQuery(id+"F2.wireOp",EDGE,"E90.left"),sQuery(id+"F2.wireOp",EDGE,"E90.right"),sQuery(id+"F2.wireOp",EDGE,"E92.MirrorCS"),sQuery(id+"F2.wireOp",EDGE,"E93.MirrorCS"),sQuery(id+"F2.wireOp",EDGE,"E94.MirrorCS"),sQuery(id+"F2.wireOp",EDGE,"E95.MirrorCS"),sQuery(id+"F2.wireOp",EDGE,"E96.MirrorCS"),sQuery(id+"F2.wireOp",EDGE,"E97.MirrorCS"),sQuery(id+"F2.wireOp",EDGE,"E98.MirrorCS"),sQuery(id+"F2.wireOp",EDGE,"E99.MirrorCS"),sQuery(id+"F2.wireOp",EDGE,"E100.MirrorCS"),sQuery(id+"F2.wireOp",EDGE,"E101.MirrorCS"),sQuery(id+"F2.wireOp",EDGE,"E107"),sQuery(id+"F2.wireOp",EDGE,"E108"),sQuery(id+"F2.wireOp",EDGE,"E109"),sQuery(id+"F2.wireOp",EDGE,"E110"),sQuery(id+"F2.wireOp",EDGE,"E111"),sQuery(id+"F2.wireOp",EDGE,"E112")])]});
            var Q1;
            Q1=makeQuery(id+"F12.opExtrude","SWEPT_BODY",BODY,{"disambiguationData":[OSD([sQuery(id+"F11.wireOp",EDGE,"E154.0.1.0"),sQuery(id+"F11.wireOp",EDGE,"E154.0.1.1"),sQuery(id+"F11.wireOp",EDGE,"E154.0.1.2"),sQuery(id+"F11.wireOp",EDGE,"E154.0.1.3")])]});
            var Q2;
            Q2=makeQuery(id+"F12.opExtrude","SWEPT_BODY",BODY,{"disambiguationData":[OSD([sQuery(id+"F11.wireOp",EDGE,"E150"),sQuery(id+"F11.wireOp",EDGE,"E152"),sQuery(id+"F11.wireOp",EDGE,"E153"),sQuery(id+"F11.wireOp",EDGE,"E151")])]});
            var Q3;
            Q3=makeQuery(id+"F13.opPattern","COPY",BODY,{"derivedFrom":makeQuery(id+"F12.opExtrude","SWEPT_BODY",BODY,{"disambiguationData":[OSD([sQuery(id+"F11.wireOp",EDGE,"E150"),sQuery(id+"F11.wireOp",EDGE,"E152"),sQuery(id+"F11.wireOp",EDGE,"E153"),sQuery(id+"F11.wireOp",EDGE,"E151")])]}),"instanceName":"1"});
            var Q4;
            Q4=makeQuery(id+"F13.opPattern","COPY",BODY,{"derivedFrom":makeQuery(id+"F12.opExtrude","SWEPT_BODY",BODY,{"disambiguationData":[OSD([sQuery(id+"F11.wireOp",EDGE,"E154.0.1.0"),sQuery(id+"F11.wireOp",EDGE,"E154.0.1.1"),sQuery(id+"F11.wireOp",EDGE,"E154.0.1.2"),sQuery(id+"F11.wireOp",EDGE,"E154.0.1.3")])]}),"instanceName":"1"});
            var Q5;
            Q5=makeQuery(id+"F13.opPattern","COPY",BODY,{"derivedFrom":makeQuery(id+"F12.opExtrude","SWEPT_BODY",BODY,{"disambiguationData":[OSD([sQuery(id+"F11.wireOp",EDGE,"E155.MirrorCS"),sQuery(id+"F11.wireOp",EDGE,"E157.MirrorCS"),sQuery(id+"F11.wireOp",EDGE,"E158.MirrorCS"),sQuery(id+"F11.wireOp",EDGE,"E148.0.1")])]}),"instanceName":"1"});
            var Q6;
            Q6=makeQuery(id+"F12.opExtrude","SWEPT_BODY",BODY,{"disambiguationData":[OSD([sQuery(id+"F11.wireOp",EDGE,"E155.MirrorCS"),sQuery(id+"F11.wireOp",EDGE,"E157.MirrorCS"),sQuery(id+"F11.wireOp",EDGE,"E158.MirrorCS"),sQuery(id+"F11.wireOp",EDGE,"E148.0.1")])]});
            booleanBodies(context, id + "F16", {"operationType" : BooleanOperationType.UNION, "tools" : qUnion([Q0, Q1, Q2, Q3, Q4, Q5, Q6])});
        }
        {
            var Q0;
            Q0=makeQuery(id+"F7.opPattern","COPY",FACE,{"derivedFrom":makeQuery(id+"F6.opExtrude","SWEPT_FACE",FACE,{"disambiguationData":[OSD([sQuery(id+"F5.wireOp",EDGE,"E127.left")])]}),"instanceName":"1"});
            var sketch = newSketch(context, id + "F17", { "sketchPlane" : qUnion([Q0])});
            skLineSegment(sketch, "E160.0", {"start": v(-100, 56) * mm, "end": v(-96, 56) * mm});
            skLineSegment(sketch, "E160.1", {"start": v(-100, 30) * mm, "end": v(-96, 30) * mm});
            skLineSegment(sketch, "E160.2", {"start": v(-100, 45) * mm, "end": v(-96, 45) * mm});
            skLineSegment(sketch, "E160.3", {"start": v(-100, 19) * mm, "end": v(-96, 19) * mm});
            skLineSegment(sketch, "E160.4", {"start": v(-100, 19) * mm, "end": v(-96, 19) * mm});
            skLineSegment(sketch, "E160.5", {"start": v(-100, 56) * mm, "end": v(-96, 56) * mm});
            skLineSegment(sketch, "E160.6", {"start": v(-100, 30) * mm, "end": v(-96, 30) * mm});
            skLineSegment(sketch, "E160.7", {"start": v(-100, 45) * mm, "end": v(-96, 45) * mm});
            skLineSegment(sketch, "E161.left", {"start": v(-100, 56) * mm, "end": v(-100, 45) * mm});
            skLineSegment(sketch, "E161.right", {"start": v(-96, 56) * mm, "end": v(-96, 45) * mm});
            skLineSegment(sketch, "E162.left", {"start": v(-100, 30) * mm, "end": v(-100, 19) * mm});
            skLineSegment(sketch, "E162.right", {"start": v(-96, 30) * mm, "end": v(-96, 19) * mm});
            skSolve(sketch);
        }
        {
            var Q0;
            Q0 = qSketchRegion(id + "F17", true);
            extrude(context, id + "F18", {"entities" : qUnion([Q0]), "depth" : 4 * mm});
        }
        {
            var Q0;
            Q0=makeQuery(id+"F18.opExtrude","SWEPT_BODY",BODY,{"disambiguationData":[OSD([sQuery(id+"F17.wireOp",EDGE,"E160.0"),sQuery(id+"F17.wireOp",EDGE,"E160.2"),sQuery(id+"F17.wireOp",EDGE,"E161.left"),sQuery(id+"F17.wireOp",EDGE,"E161.right")])]});
            var Q1;
            Q1=makeQuery(id+"F18.opExtrude","SWEPT_BODY",BODY,{"disambiguationData":[OSD([sQuery(id+"F17.wireOp",EDGE,"E160.1"),sQuery(id+"F17.wireOp",EDGE,"E160.3"),sQuery(id+"F17.wireOp",EDGE,"E162.left"),sQuery(id+"F17.wireOp",EDGE,"E162.right")])]});
            var Q2;
            Q2=qCreatedBy(makeId("Front.planeOp"),FACE);
            mirror(context, id + "F19", {"entities" : qUnion([Q0, Q1]), "mirrorPlane" : qUnion([Q2])});
        }
        {
            var Q0;
            Q0=makeQuery(id+"F18.opExtrude","SWEPT_BODY",BODY,{"disambiguationData":[OSD([sQuery(id+"F17.wireOp",EDGE,"E160.0"),sQuery(id+"F17.wireOp",EDGE,"E160.2"),sQuery(id+"F17.wireOp",EDGE,"E161.left"),sQuery(id+"F17.wireOp",EDGE,"E161.right")])]});
            var Q1;
            Q1=makeQuery(id+"F7.opPattern","COPY",BODY,{"derivedFrom":makeQuery(id+"F6.opExtrude","SWEPT_BODY",BODY,{"disambiguationData":[OSD([sQuery(id+"F5.wireOp",EDGE,"E118.0.0"),sQuery(id+"F5.wireOp",EDGE,"E118.0.1"),sQuery(id+"F5.wireOp",EDGE,"E118.0.3"),sQuery(id+"F5.wireOp",EDGE,"E119.0.0"),sQuery(id+"F5.wireOp",EDGE,"E119.0.1"),sQuery(id+"F5.wireOp",EDGE,"E119.0.3"),sQuery(id+"F5.wireOp",EDGE,"E120.0.0"),sQuery(id+"F5.wireOp",EDGE,"E120.0.1"),sQuery(id+"F5.wireOp",EDGE,"E120.0.3"),sQuery(id+"F5.wireOp",EDGE,"E121.0.0"),sQuery(id+"F5.wireOp",EDGE,"E121.0.1"),sQuery(id+"F5.wireOp",EDGE,"E121.0.3"),sQuery(id+"F5.wireOp",EDGE,"E122.0.0"),sQuery(id+"F5.wireOp",EDGE,"E122.0.1"),sQuery(id+"F5.wireOp",EDGE,"E122.0.3"),sQuery(id+"F5.wireOp",EDGE,"E116.bottom"),sQuery(id+"F5.wireOp",EDGE,"E127.top"),sQuery(id+"F5.wireOp",EDGE,"E127.left"),sQuery(id+"F5.wireOp",EDGE,"E127.right"),sQuery(id+"F5.wireOp",EDGE,"E129.MirrorCS"),sQuery(id+"F5.wireOp",EDGE,"E130.MirrorCS"),sQuery(id+"F5.wireOp",EDGE,"E131.MirrorCS"),sQuery(id+"F5.wireOp",EDGE,"E132.MirrorCS"),sQuery(id+"F5.wireOp",EDGE,"E133.MirrorCS"),sQuery(id+"F5.wireOp",EDGE,"E134.MirrorCS"),sQuery(id+"F5.wireOp",EDGE,"E135.MirrorCS"),sQuery(id+"F5.wireOp",EDGE,"E136.MirrorCS"),sQuery(id+"F5.wireOp",EDGE,"E137.MirrorCS"),sQuery(id+"F5.wireOp",EDGE,"E138.MirrorCS"),sQuery(id+"F5.wireOp",EDGE,"E139"),sQuery(id+"F5.wireOp",EDGE,"E140"),sQuery(id+"F5.wireOp",EDGE,"E141"),sQuery(id+"F5.wireOp",EDGE,"E142"),sQuery(id+"F5.wireOp",EDGE,"E143"),sQuery(id+"F5.wireOp",EDGE,"E144")])]}),"instanceName":"1"});
            var Q2;
            Q2=makeQuery(id+"F18.opExtrude","SWEPT_BODY",BODY,{"disambiguationData":[OSD([sQuery(id+"F17.wireOp",EDGE,"E160.1"),sQuery(id+"F17.wireOp",EDGE,"E160.3"),sQuery(id+"F17.wireOp",EDGE,"E162.left"),sQuery(id+"F17.wireOp",EDGE,"E162.right")])]});
            var Q3;
            Q3=makeQuery(id+"F19.opPattern","COPY",BODY,{"derivedFrom":makeQuery(id+"F18.opExtrude","SWEPT_BODY",BODY,{"disambiguationData":[OSD([sQuery(id+"F17.wireOp",EDGE,"E160.1"),sQuery(id+"F17.wireOp",EDGE,"E160.3"),sQuery(id+"F17.wireOp",EDGE,"E162.left"),sQuery(id+"F17.wireOp",EDGE,"E162.right")])]}),"instanceName":"1"});
            var Q4;
            Q4=makeQuery(id+"F19.opPattern","COPY",BODY,{"derivedFrom":makeQuery(id+"F18.opExtrude","SWEPT_BODY",BODY,{"disambiguationData":[OSD([sQuery(id+"F17.wireOp",EDGE,"E160.0"),sQuery(id+"F17.wireOp",EDGE,"E160.2"),sQuery(id+"F17.wireOp",EDGE,"E161.left"),sQuery(id+"F17.wireOp",EDGE,"E161.right")])]}),"instanceName":"1"});
            var Q5;
            Q5=qCreatedBy(makeId("Right.planeOp"),FACE);
            mirror(context, id + "F20", {"entities" : qUnion([Q0, Q1, Q2, Q3, Q4]), "mirrorPlane" : qUnion([Q5])});
        }
        {
            var Q0;
            Q0=makeQuery(id+"F10.imprint","IMPRINT",FACE,{"disambiguationData":[TD([[makeQuery(id+"F10.imprint","IMPRINT",EDGE,{"derivedFrom":makeQuery(id+"F6.opExtrude","CAP_EDGE",EDGE,{"disambiguationData":[OSD([sQuery(id+"F5.wireOp",EDGE,"E118.0.0")])],"isStart":false})}),1.0]])]});
            var sketch = newSketch(context, id + "F21", { "sketchPlane" : qUnion([Q0])});
            skLineSegment(sketch, "E163.bottom", {"start": v(75, 55) * mm, "end": v(-75, 55) * mm});
            skLineSegment(sketch, "E163.top", {"start": v(75, 40) * mm, "end": v(-75, 40) * mm});
            skLineSegment(sketch, "E163.left", {"start": v(75, 55) * mm, "end": v(75, 40) * mm});
            skLineSegment(sketch, "E163.right", {"start": v(-75, 55) * mm, "end": v(-75, 40) * mm});
            skPoint(sketch, "E163.middle", {"position": v(0, 47.5) * mm});
            skSolve(sketch);
        }
        {
            var Q0;
            Q0 = qSketchRegion(id + "F21", true);
            extrude(context, id + "F22", {"entities" : qUnion([Q0]), "operationType" : NewBodyOperationType.REMOVE, "oppositeDirection" : true, "depth" : 4 * mm});
        }
    });
